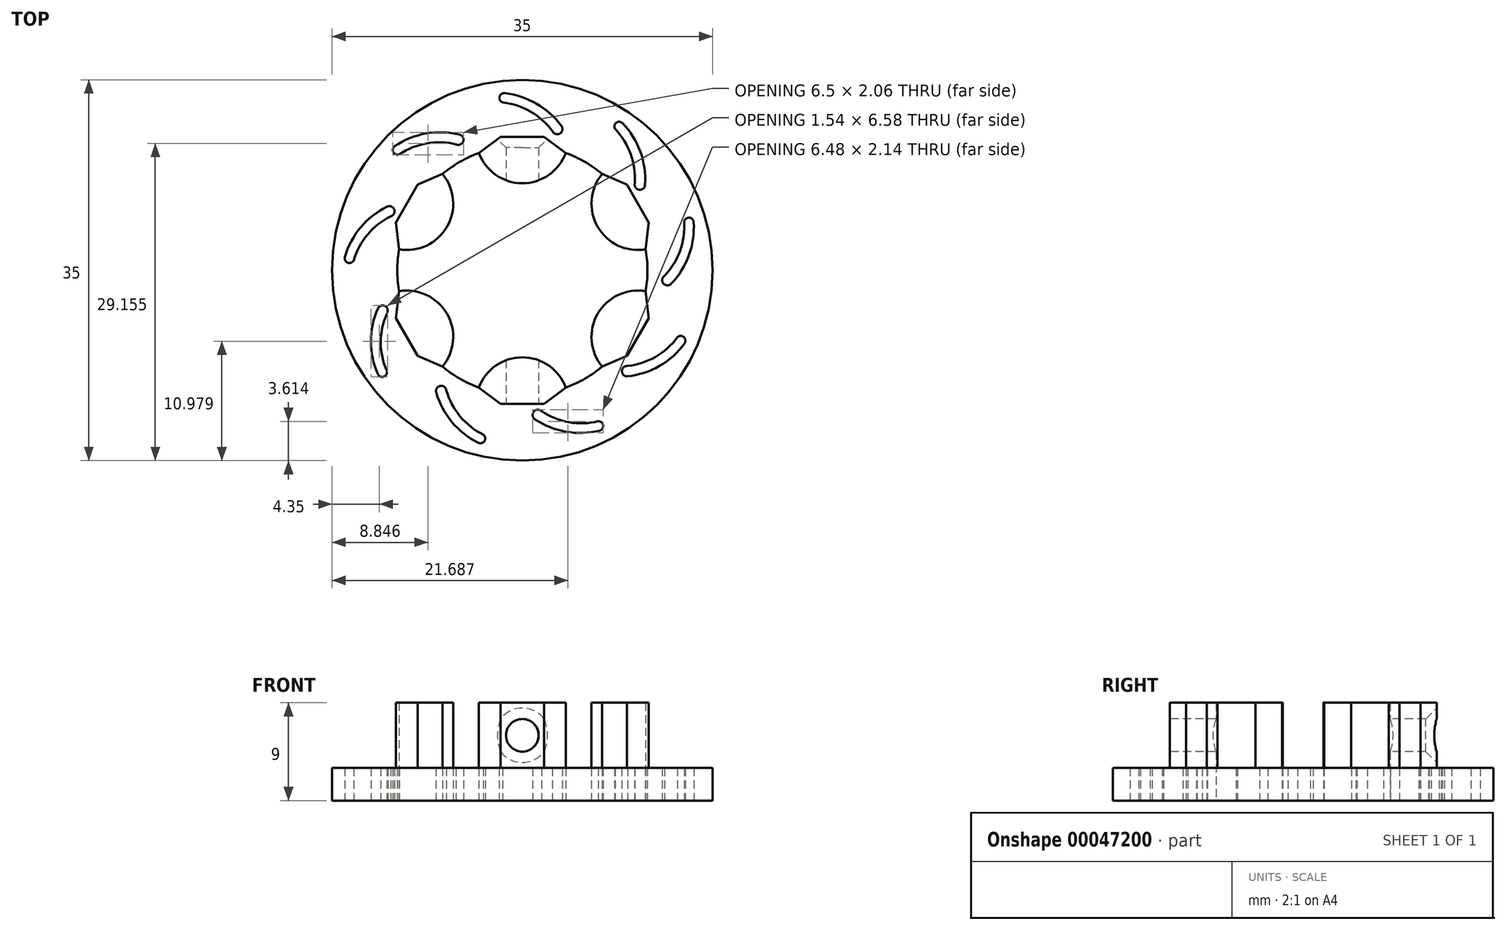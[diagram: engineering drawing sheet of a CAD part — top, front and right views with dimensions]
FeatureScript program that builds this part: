
annotation { "Feature Type Name" : "Feature", "Feature Type Description" : "" }
export const myFeature = defineFeature(function(context is Context, id is Id, definition is map)
    precondition{}
    {
        {
            var Q0;
            Q0=qCreatedBy(makeId("Top.planeOp"),FACE);
            var sketch = newSketch(context, id + "F0", { "sketchPlane" : qUnion([Q0])});
            skCircle(sketch, "E0", {"center": v(0, 0) * mm, "radius": 8.5 * mm});
            skCircle(sketch, "E1", {"center": v(0, 0) * mm, "radius": 11.5 * mm});
            skCircle(sketch, "E2", {"center": v(0, 8.5) * mm, "radius": 1.8 * mm});
            skCircle(sketch, "E3.1.0", {"center": v(-7.36, 4.25) * mm, "radius": 1.8 * mm});
            skCircle(sketch, "E3.2.0", {"center": v(-7.36, -4.25) * mm, "radius": 1.8 * mm});
            skCircle(sketch, "E3.3.0", {"center": v(0, -8.5) * mm, "radius": 1.8 * mm});
            skCircle(sketch, "E3.4.0", {"center": v(7.36, -4.25) * mm, "radius": 1.8 * mm});
            skCircle(sketch, "E3.5.0", {"center": v(7.36, 4.25) * mm, "radius": 1.8 * mm});
            skCircle(sketch, "E4", {"center": v(0, 0) * mm, "radius": 17.5 * mm});
            skSolve(sketch);
        }
        {
            var Q0;
            Q0=makeQuery(id+"F0.imprint","IMPRINT",FACE,{"disambiguationData":[TD([[makeQuery(id+"F0.imprint","IMPRINT",EDGE,{"derivedFrom":sQuery(id+"F0.wireOp",EDGE,"E1")}),-1.0]])]});
            extrude(context, id + "F1", {"entities" : qUnion([Q0]), "depth" : 3 * mm});
        }
        {
            var Q0;
            Q0=qCreatedBy(makeId("Top.planeOp"),FACE);
            var sketch = newSketch(context, id + "F2", { "sketchPlane" : qUnion([Q0])});
            skArc(sketch, "E5", {"start": v(3.6, 13.27) * mm, "mid": v(1.3, 15.32) * mm, "end": v(-1.63, 16.28) * mm});
            skArc(sketch, "E6", {"start": v(2.77, 12.79) * mm, "mid": v(0.76, 14.59) * mm, "end": v(-1.8, 15.43) * mm});
            skArc(sketch, "E7", {"start": v(-1.63, 16.28) * mm, "mid": v(-2.1, 15.93) * mm, "end": v(-1.8, 15.43) * mm});
            skArc(sketch, "E8", {"start": v(3.6, 13.27) * mm, "mid": v(3.45, 12.57) * mm, "end": v(2.77, 12.79) * mm});
            skArc(sketch, "E9.1.0", {"start": v(-5.77, 12.48) * mm, "mid": v(-8.85, 12.58) * mm, "end": v(-11.71, 11.43) * mm});
            skArc(sketch, "E9.1.1", {"start": v(-6.1, 11.58) * mm, "mid": v(-8.8, 11.66) * mm, "end": v(-11.3, 10.66) * mm});
            skArc(sketch, "E9.1.2", {"start": v(-5.77, 12.48) * mm, "mid": v(-5.43, 11.85) * mm, "end": v(-6.1, 11.58) * mm});
            skArc(sketch, "E9.1.3", {"start": v(-11.71, 11.43) * mm, "mid": v(-11.85, 10.85) * mm, "end": v(-11.3, 10.66) * mm});
            skArc(sketch, "E9.2.0", {"start": v(-12.44, 5.85) * mm, "mid": v(-14.86, 3.94) * mm, "end": v(-16.32, 1.23) * mm});
            skArc(sketch, "E9.2.1", {"start": v(-12.11, 4.95) * mm, "mid": v(-14.23, 3.28) * mm, "end": v(-15.5, 0.9) * mm});
            skArc(sketch, "E9.2.2", {"start": v(-12.44, 5.85) * mm, "mid": v(-11.78, 5.58) * mm, "end": v(-12.11, 4.95) * mm});
            skArc(sketch, "E9.2.3", {"start": v(-16.32, 1.23) * mm, "mid": v(-16.06, 0.7) * mm, "end": v(-15.5, 0.9) * mm});
            skArc(sketch, "E9.3.0", {"start": v(-13.29, -3.52) * mm, "mid": v(-13.92, -6.53) * mm, "end": v(-13.29, -9.55) * mm});
            skArc(sketch, "E9.3.1", {"start": v(-12.46, -4) * mm, "mid": v(-13.01, -6.63) * mm, "end": v(-12.46, -9.28) * mm});
            skArc(sketch, "E9.3.2", {"start": v(-13.29, -3.52) * mm, "mid": v(-12.6, -3.3) * mm, "end": v(-12.46, -4) * mm});
            skArc(sketch, "E9.3.3", {"start": v(-13.29, -9.55) * mm, "mid": v(-12.75, -9.79) * mm, "end": v(-12.46, -9.28) * mm});
            skArc(sketch, "E9.4.0", {"start": v(-7.92, -11.24) * mm, "mid": v(-6.47, -13.95) * mm, "end": v(-4.04, -15.86) * mm});
            skArc(sketch, "E9.4.1", {"start": v(-6.98, -11.07) * mm, "mid": v(-5.7, -13.45) * mm, "end": v(-3.58, -15.11) * mm});
            skArc(sketch, "E9.4.2", {"start": v(-7.92, -11.24) * mm, "mid": v(-7.54, -10.63) * mm, "end": v(-6.98, -11.07) * mm});
            skArc(sketch, "E9.4.3", {"start": v(-4.04, -15.86) * mm, "mid": v(-3.47, -15.7) * mm, "end": v(-3.58, -15.11) * mm});
            skArc(sketch, "E9.5.0", {"start": v(1.16, -13.7) * mm, "mid": v(4.02, -14.84) * mm, "end": v(7.1, -14.74) * mm});
            skArc(sketch, "E9.5.1", {"start": v(1.77, -12.96) * mm, "mid": v(4.27, -13.97) * mm, "end": v(6.97, -13.88) * mm});
            skArc(sketch, "E9.5.2", {"start": v(1.16, -13.7) * mm, "mid": v(1.05, -12.99) * mm, "end": v(1.77, -12.96) * mm});
            skArc(sketch, "E9.5.3", {"start": v(7.1, -14.74) * mm, "mid": v(7.43, -14.25) * mm, "end": v(6.97, -13.88) * mm});
            skArc(sketch, "E9.6.0", {"start": v(9.69, -9.75) * mm, "mid": v(12.62, -8.79) * mm, "end": v(14.91, -6.73) * mm});
            skArc(sketch, "E9.6.1", {"start": v(9.69, -8.8) * mm, "mid": v(12.25, -7.95) * mm, "end": v(14.26, -6.15) * mm});
            skArc(sketch, "E9.6.2", {"start": v(9.69, -9.75) * mm, "mid": v(9.16, -9.27) * mm, "end": v(9.69, -8.8) * mm});
            skArc(sketch, "E9.6.3", {"start": v(14.91, -6.73) * mm, "mid": v(14.85, -6.15) * mm, "end": v(14.26, -6.15) * mm});
            skArc(sketch, "E9.7.0", {"start": v(13.69, -1.24) * mm, "mid": v(15.32, 1.38) * mm, "end": v(15.75, 4.43) * mm});
            skArc(sketch, "E9.7.1", {"start": v(13.07, -0.5) * mm, "mid": v(14.5, 1.78) * mm, "end": v(14.88, 4.46) * mm});
            skArc(sketch, "E9.7.2", {"start": v(13.69, -1.24) * mm, "mid": v(12.98, -1.22) * mm, "end": v(13.07, -0.5) * mm});
            skArc(sketch, "E9.7.3", {"start": v(15.75, 4.43) * mm, "mid": v(15.33, 4.84) * mm, "end": v(14.88, 4.46) * mm});
            skArc(sketch, "E9.8.0", {"start": v(11.28, 7.85) * mm, "mid": v(10.85, 10.9) * mm, "end": v(9.22, 13.52) * mm});
            skArc(sketch, "E9.8.1", {"start": v(10.34, 8.01) * mm, "mid": v(9.96, 10.69) * mm, "end": v(8.53, 12.98) * mm});
            skArc(sketch, "E9.8.2", {"start": v(11.28, 7.85) * mm, "mid": v(10.72, 7.4) * mm, "end": v(10.34, 8.01) * mm});
            skArc(sketch, "E9.8.3", {"start": v(9.22, 13.52) * mm, "mid": v(8.63, 13.56) * mm, "end": v(8.53, 12.98) * mm});
            skPoint(sketch, "E9.center", {"position": v(0, 0) * mm});
            skSolve(sketch);
        }
        {
            var Q0;
            Q0=makeQuery(id+"F2.imprint","IMPRINT",FACE,{"disambiguationData":[TD([[makeQuery(id+"F2.imprint","IMPRINT",EDGE,{"derivedFrom":sQuery(id+"F2.wireOp",EDGE,"E9.8.0")}),1.0]])]});
            var Q1;
            Q1=makeQuery(id+"F2.imprint","IMPRINT",FACE,{"disambiguationData":[TD([[makeQuery(id+"F2.imprint","IMPRINT",EDGE,{"derivedFrom":sQuery(id+"F2.wireOp",EDGE,"E5")}),1.0]])]});
            var Q2;
            Q2=makeQuery(id+"F2.imprint","IMPRINT",FACE,{"disambiguationData":[TD([[makeQuery(id+"F2.imprint","IMPRINT",EDGE,{"derivedFrom":sQuery(id+"F2.wireOp",EDGE,"E9.1.0")}),1.0]])]});
            var Q3;
            Q3=makeQuery(id+"F2.imprint","IMPRINT",FACE,{"disambiguationData":[TD([[makeQuery(id+"F2.imprint","IMPRINT",EDGE,{"derivedFrom":sQuery(id+"F2.wireOp",EDGE,"E9.2.0")}),1.0]])]});
            var Q4;
            Q4=makeQuery(id+"F2.imprint","IMPRINT",FACE,{"disambiguationData":[TD([[makeQuery(id+"F2.imprint","IMPRINT",EDGE,{"derivedFrom":sQuery(id+"F2.wireOp",EDGE,"E9.3.0")}),1.0]])]});
            var Q5;
            Q5=makeQuery(id+"F2.imprint","IMPRINT",FACE,{"disambiguationData":[TD([[makeQuery(id+"F2.imprint","IMPRINT",EDGE,{"derivedFrom":sQuery(id+"F2.wireOp",EDGE,"E9.4.0")}),1.0]])]});
            var Q6;
            Q6=makeQuery(id+"F2.imprint","IMPRINT",FACE,{"disambiguationData":[TD([[makeQuery(id+"F2.imprint","IMPRINT",EDGE,{"derivedFrom":sQuery(id+"F2.wireOp",EDGE,"E9.5.0")}),1.0]])]});
            var Q7;
            Q7=makeQuery(id+"F2.imprint","IMPRINT",FACE,{"disambiguationData":[TD([[makeQuery(id+"F2.imprint","IMPRINT",EDGE,{"derivedFrom":sQuery(id+"F2.wireOp",EDGE,"E9.6.0")}),1.0]])]});
            var Q8;
            Q8=makeQuery(id+"F2.imprint","IMPRINT",FACE,{"disambiguationData":[TD([[makeQuery(id+"F2.imprint","IMPRINT",EDGE,{"derivedFrom":sQuery(id+"F2.wireOp",EDGE,"E9.7.0")}),1.0]])]});
            extrude(context, id + "F3", {"entities" : qUnion([Q0, Q1, Q2, Q3, Q4, Q5, Q6, Q7, Q8]), "operationType" : NewBodyOperationType.REMOVE, "endBound" : BoundingType.THROUGH_ALL, "depth" : 25 * mm});
        }
        {
            var Q0;
            Q0=makeQuery(id+"F1.opExtrude","CAP_FACE",FACE,{"disambiguationData":[OSD([sQuery(id+"F0.wireOp",EDGE,"E1"),sQuery(id+"F0.wireOp",EDGE,"E4")])],"isStart":false});
            var sketch = newSketch(context, id + "F4", { "sketchPlane" : qUnion([Q0])});
            skCircle(sketch, "E10", {"center": v(0, 0) * mm, "radius": 7 * mm});
            skLineSegment(sketch, "E11", {"start": v(-0.06, 5.7) * mm, "end": v(-4.06, 5.7) * mm});
            skLineSegment(sketch, "E12", {"start": v(-0.06, 5.7) * mm, "end": v(4.06, 5.7) * mm});
            skLineSegment(sketch, "E13", {"start": v(-0.06, 7) * mm, "end": v(-0.06, 3.5) * mm});
            skArc(sketch, "E14", {"start": v(-4.06, 5.7) * mm, "mid": v(0, 3.5) * mm, "end": v(4.06, 5.7) * mm});
            skCircle(sketch, "E15", {"center": v(0, 0) * mm, "radius": 11.5 * mm});
            skArc(sketch, "E16", {"start": v(-4, 10.78) * mm, "mid": v(0, 8) * mm, "end": v(4, 10.78) * mm});
            skArc(sketch, "E17.1.0", {"start": v(-11.34, 1.93) * mm, "mid": v(-6.93, 4) * mm, "end": v(-7.34, 8.86) * mm});
            skArc(sketch, "E17.2.0", {"start": v(-7.34, -8.86) * mm, "mid": v(-6.93, -4) * mm, "end": v(-11.34, -1.93) * mm});
            skArc(sketch, "E17.3.0", {"start": v(4, -10.78) * mm, "mid": v(0, -8) * mm, "end": v(-4, -10.78) * mm});
            skArc(sketch, "E17.4.0", {"start": v(11.34, -1.93) * mm, "mid": v(6.93, -4) * mm, "end": v(7.34, -8.86) * mm});
            skArc(sketch, "E17.5.0", {"start": v(7.34, 8.86) * mm, "mid": v(6.93, 4) * mm, "end": v(11.34, 1.93) * mm});
            skLineSegment(sketch, "E18", {"start": v(0, 12.27) * mm, "end": v(2, 12.27) * mm});
            skLineSegment(sketch, "E19", {"start": v(2, 12.27) * mm, "end": v(4, 10.78) * mm});
            skLineSegment(sketch, "E20", {"start": v(0, 12.27) * mm, "end": v(-2, 12.27) * mm});
            skLineSegment(sketch, "E21", {"start": v(-2, 12.27) * mm, "end": v(-4, 10.78) * mm});
            skLineSegment(sketch, "E22.1.0", {"start": v(-10.62, 6.13) * mm, "end": v(-9.62, 7.87) * mm});
            skLineSegment(sketch, "E22.1.1", {"start": v(-10.62, 6.13) * mm, "end": v(-11.62, 4.4) * mm});
            skLineSegment(sketch, "E22.1.2", {"start": v(-11.62, 4.4) * mm, "end": v(-11.34, 1.93) * mm});
            skLineSegment(sketch, "E22.1.3", {"start": v(-9.62, 7.87) * mm, "end": v(-7.34, 8.86) * mm});
            skLineSegment(sketch, "E22.2.0", {"start": v(-10.62, -6.13) * mm, "end": v(-11.62, -4.4) * mm});
            skLineSegment(sketch, "E22.2.1", {"start": v(-10.62, -6.13) * mm, "end": v(-9.62, -7.87) * mm});
            skLineSegment(sketch, "E22.2.2", {"start": v(-9.62, -7.87) * mm, "end": v(-7.34, -8.86) * mm});
            skLineSegment(sketch, "E22.2.3", {"start": v(-11.62, -4.4) * mm, "end": v(-11.34, -1.93) * mm});
            skLineSegment(sketch, "E23.1.3.0", {"start": v(0, -12.27) * mm, "end": v(-2, -12.27) * mm});
            skLineSegment(sketch, "E23.3.3.0", {"start": v(0, -12.27) * mm, "end": v(2, -12.27) * mm});
            skLineSegment(sketch, "E23.6.3.0", {"start": v(2, -12.27) * mm, "end": v(4, -10.78) * mm});
            skLineSegment(sketch, "E23.9.3.0", {"start": v(-2, -12.27) * mm, "end": v(-4, -10.78) * mm});
            skLineSegment(sketch, "E23.1.4.0", {"start": v(10.62, -6.13) * mm, "end": v(9.62, -7.87) * mm});
            skLineSegment(sketch, "E23.3.4.0", {"start": v(10.62, -6.13) * mm, "end": v(11.62, -4.4) * mm});
            skLineSegment(sketch, "E23.6.4.0", {"start": v(11.62, -4.4) * mm, "end": v(11.34, -1.93) * mm});
            skLineSegment(sketch, "E23.9.4.0", {"start": v(9.62, -7.87) * mm, "end": v(7.34, -8.86) * mm});
            skLineSegment(sketch, "E23.1.5.0", {"start": v(10.62, 6.13) * mm, "end": v(11.62, 4.4) * mm});
            skLineSegment(sketch, "E23.3.5.0", {"start": v(10.62, 6.13) * mm, "end": v(9.62, 7.87) * mm});
            skLineSegment(sketch, "E23.6.5.0", {"start": v(9.62, 7.87) * mm, "end": v(7.34, 8.86) * mm});
            skLineSegment(sketch, "E23.9.5.0", {"start": v(11.62, 4.4) * mm, "end": v(11.34, 1.93) * mm});
            skSolve(sketch);
        }
        {
            var Q0;
            {var subQ0=sQuery(id+"F4.wireOp",EDGE,"E16");Q0=makeQuery(id+"F4.imprint","IMPRINT",FACE,{"disambiguationData":[TD([[makeQuery(id+"F4.imprint","IMPRINT",EDGE,{"derivedFrom":subQ0}),1.0]])]});}
            var Q1;
            {var subQ0=sQuery(id+"F4.wireOp",EDGE,"E17.5.0");Q1=makeQuery(id+"F4.imprint","IMPRINT",FACE,{"disambiguationData":[TD([[makeQuery(id+"F4.imprint","IMPRINT",EDGE,{"derivedFrom":subQ0}),1.0]])]});}
            var Q2;
            {var subQ0=sQuery(id+"F4.wireOp",EDGE,"E17.4.0");Q2=makeQuery(id+"F4.imprint","IMPRINT",FACE,{"disambiguationData":[TD([[makeQuery(id+"F4.imprint","IMPRINT",EDGE,{"derivedFrom":subQ0}),1.0]])]});}
            var Q3;
            {var subQ0=sQuery(id+"F4.wireOp",EDGE,"E17.3.0");Q3=makeQuery(id+"F4.imprint","IMPRINT",FACE,{"disambiguationData":[TD([[makeQuery(id+"F4.imprint","IMPRINT",EDGE,{"derivedFrom":subQ0}),1.0]])]});}
            var Q4;
            {var subQ0=sQuery(id+"F4.wireOp",EDGE,"E17.2.0");Q4=makeQuery(id+"F4.imprint","IMPRINT",FACE,{"disambiguationData":[TD([[makeQuery(id+"F4.imprint","IMPRINT",EDGE,{"derivedFrom":subQ0}),1.0]])]});}
            var Q5;
            {var subQ0=sQuery(id+"F4.wireOp",EDGE,"E17.1.0");Q5=makeQuery(id+"F4.imprint","IMPRINT",FACE,{"disambiguationData":[TD([[makeQuery(id+"F4.imprint","IMPRINT",EDGE,{"derivedFrom":subQ0}),1.0]])]});}
            var Q6;
            Q6=makeQuery(id+"F4.imprint","IMPRINT",FACE,{"disambiguationData":[TD([[makeQuery(id+"F4.imprint","IMPRINT",EDGE,{"derivedFrom":sQuery(id+"F4.wireOp",EDGE,"E18")}),-1.0]])]});
            var Q7;
            Q7=makeQuery(id+"F4.imprint","IMPRINT",FACE,{"disambiguationData":[TD([[makeQuery(id+"F4.imprint","IMPRINT",EDGE,{"derivedFrom":sQuery(id+"F4.wireOp",EDGE,"E23.1.5.0")}),-1.0]])]});
            var Q8;
            Q8=makeQuery(id+"F4.imprint","IMPRINT",FACE,{"disambiguationData":[TD([[makeQuery(id+"F4.imprint","IMPRINT",EDGE,{"derivedFrom":sQuery(id+"F4.wireOp",EDGE,"E23.1.4.0")}),-1.0]])]});
            var Q9;
            Q9=makeQuery(id+"F4.imprint","IMPRINT",FACE,{"disambiguationData":[TD([[makeQuery(id+"F4.imprint","IMPRINT",EDGE,{"derivedFrom":sQuery(id+"F4.wireOp",EDGE,"E23.1.3.0")}),-1.0]])]});
            var Q10;
            Q10=makeQuery(id+"F4.imprint","IMPRINT",FACE,{"disambiguationData":[TD([[makeQuery(id+"F4.imprint","IMPRINT",EDGE,{"derivedFrom":sQuery(id+"F4.wireOp",EDGE,"E22.2.0")}),-1.0]])]});
            var Q11;
            Q11=makeQuery(id+"F4.imprint","IMPRINT",FACE,{"disambiguationData":[TD([[makeQuery(id+"F4.imprint","IMPRINT",EDGE,{"derivedFrom":sQuery(id+"F4.wireOp",EDGE,"E22.1.0")}),-1.0]])]});
            extrude(context, id + "F5", {"entities" : qUnion([Q0, Q1, Q2, Q3, Q4, Q5, Q6, Q7, Q8, Q9, Q10, Q11]), "operationType" : NewBodyOperationType.ADD, "depth" : 6 * mm, "hasSecondDirection" : true, "secondDirectionOppositeDirection" : true, "secondDirectionDepth" : 3 * mm});
        }
        {
            var Q0;
            Q0=makeQuery(id+"F5.opExtrude","SWEPT_FACE",FACE,{"disambiguationData":[OSD([sQuery(id+"F4.wireOp",EDGE,"E23.1.3.0"),sQuery(id+"F4.wireOp",EDGE,"E23.3.3.0")])]});
            var sketch = newSketch(context, id + "F6", { "sketchPlane" : qUnion([Q0])});
            skCircle(sketch, "E24", {"center": v(0, 6) * mm, "radius": 1.5 * mm});
            skPoint(sketch, "E24.centerSnap0", {"position": v(0, 9) * mm});
            skPoint(sketch, "E24.centerSnap1", {"position": v(-2, 6) * mm});
            skSolve(sketch);
        }
        {
            var Q0;
            Q0=makeQuery(id+"F6.imprint","IMPRINT",FACE,{"disambiguationData":[TD([[makeQuery(id+"F6.imprint","IMPRINT",EDGE,{"derivedFrom":sQuery(id+"F6.wireOp",EDGE,"E24")}),1.0]])]});
            extrude(context, id + "F7", {"entities" : qUnion([Q0]), "operationType" : NewBodyOperationType.REMOVE, "endBound" : BoundingType.THROUGH_ALL, "oppositeDirection" : true, "depth" : 25 * mm});
        }
        {
            var Q0;
            Q0=makeQuery(id+"F7.boolean.opBoolean","COPY",EDGE,{"derivedFrom":makeQuery(id+"F7.opExtrude","CAP_EDGE",EDGE,{"disambiguationData":[OSD([sQuery(id+"F6.wireOp",EDGE,"E24")])],"isStart":true})});
            var Q1;
            Q1=makeQuery(id+"F7.boolean.opBoolean","INTERSECT",EDGE,{"derivedFrom":[makeQuery(id+"F5.opExtrude","SWEPT_FACE",FACE,{"disambiguationData":[OSD([sQuery(id+"F4.wireOp",EDGE,"E18"),sQuery(id+"F4.wireOp",EDGE,"E20")])]}),makeQuery(id+"F7.opExtrude","SWEPT_FACE",FACE,{"disambiguationData":[OSD([sQuery(id+"F6.wireOp",EDGE,"E24")])]})]});
            chamfer(context, id + "F8", {"entities" : qUnion([Q0, Q1]), "width" : 1 * mm, "tangentPropagation" : true});
        }
    });
